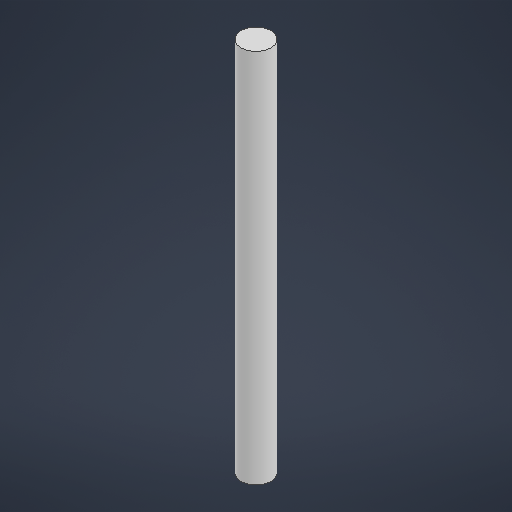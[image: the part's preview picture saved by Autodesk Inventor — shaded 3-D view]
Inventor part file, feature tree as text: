
AUTODESK INVENTOR PART (.ipt)
format: ipt  version: 2025.1 (Build 291241000, 241)  size: 191,488 bytes
history: native  units: mm
features: extrude x1, sketch x1
ambient origin geometry x8: Origin, YZ Plane, XZ Plane, XY Plane, X Axis, Y Axis, Z Axis, Center Point
bodies: Solid1 (feature_tree)
feature tree (2):
  extrude  "Extrusion1"  Depth=100.0mm TaperAngle=0.0deg
  sketch  "Sketch1"  dims[d0=8.0mm d1=100.0mm d2=0.0mm]
